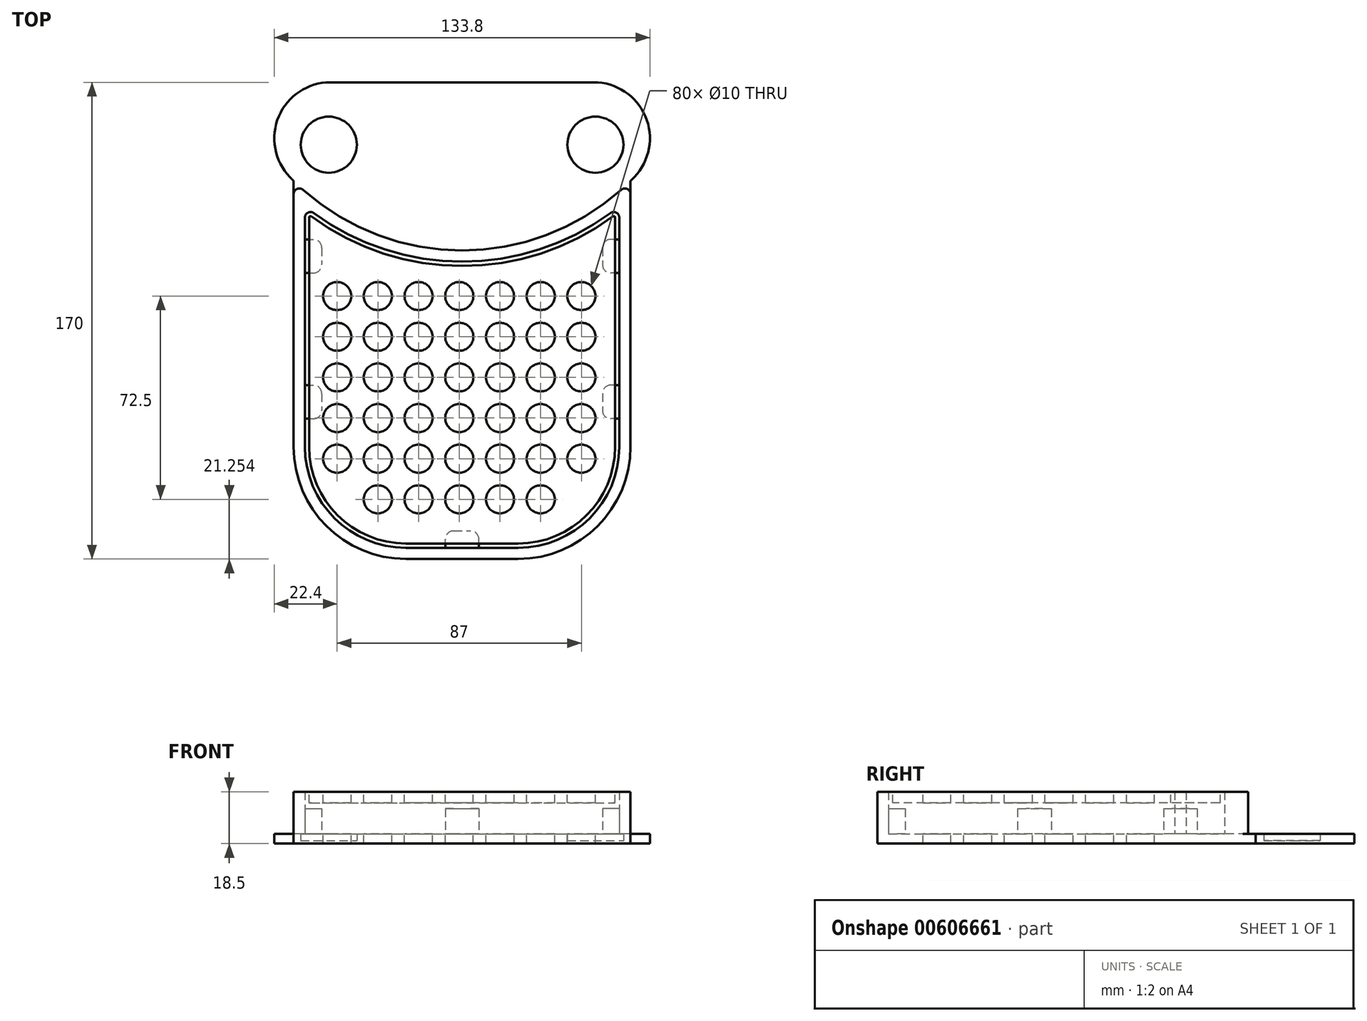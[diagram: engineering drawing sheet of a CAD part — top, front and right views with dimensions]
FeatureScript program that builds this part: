
annotation { "Feature Type Name" : "Feature", "Feature Type Description" : "" }
export const myFeature = defineFeature(function(context is Context, id is Id, definition is map)
    precondition{}
    {
        {
            var Q0;
            Q0=qCreatedBy(makeId("Top.planeOp"),FACE);
            var sketch = newSketch(context, id + "F0", { "sketchPlane" : qUnion([Q0])});
            skArc(sketch, "E0", {"start": v(-61.34, -58.85) * mm, "mid": v(-60.67, -59.53) * mm, "end": v(-60, -60.2) * mm});
            skCircle(sketch, "E1", {"center": v(-47.5, -47.25) * mm, "radius": 10 * mm});
            skCircle(sketch, "E2", {"center": v(47.5, -47.25) * mm, "radius": 10 * mm});
            skLineSegment(sketch, "E3", {"start": v(-60, -60.2) * mm, "end": v(-60, -155) * mm});
            skLineSegment(sketch, "E4", {"start": v(-20, -195) * mm, "end": v(20, -195) * mm});
            skLineSegment(sketch, "E5", {"start": v(60, -155) * mm, "end": v(60, -60.2) * mm});
            skLineSegment(sketch, "E6", {"start": v(-46.9, -25) * mm, "end": v(46.9, -25) * mm});
            skPoint(sketch, "E7.visualSharp", {"position": v(-81.24, -25) * mm});
            skArc(sketch, "E7.filletArc", {"start": v(-46.9, -25) * mm, "mid": v(-65.3, -37.16) * mm, "end": v(-61.34, -58.85) * mm});
            skPoint(sketch, "E8.visualSharp", {"position": v(81.24, -25) * mm});
            skArc(sketch, "E8.filletArc", {"start": v(61.34, -58.85) * mm, "mid": v(65.3, -37.16) * mm, "end": v(46.9, -25) * mm});
            skArc(sketch, "E9.trimOffspring", {"start": v(60, -60.2) * mm, "mid": v(60.67, -59.53) * mm, "end": v(61.34, -58.85) * mm});
            skPoint(sketch, "E10.visualSharp", {"position": v(-60, -195) * mm});
            skArc(sketch, "E10.filletArc", {"start": v(-60, -155) * mm, "mid": v(-48.28, -183.28) * mm, "end": v(-20, -195) * mm});
            skPoint(sketch, "E11.visualSharp", {"position": v(60, -195) * mm});
            skArc(sketch, "E11.filletArc", {"start": v(20, -195) * mm, "mid": v(48.28, -183.28) * mm, "end": v(60, -155) * mm});
            skSolve(sketch);
        }
        {
            var Q0;
            Q0 = qSketchRegion(id + "F0", true);
            extrude(context, id + "F1", {"entities" : qUnion([Q0]), "depth" : 3.5 * mm, "offsetDistance" : 25 * mm});
        }
        {
            var Q0;
            Q0=makeQuery(id+"F1.opExtrude","CAP_FACE",FACE,{"disambiguationData":[OSD([sQuery(id+"F0.wireOp",EDGE,"E0"),sQuery(id+"F0.wireOp",EDGE,"E1"),sQuery(id+"F0.wireOp",EDGE,"E2"),sQuery(id+"F0.wireOp",EDGE,"E3"),sQuery(id+"F0.wireOp",EDGE,"E4"),sQuery(id+"F0.wireOp",EDGE,"E5"),sQuery(id+"F0.wireOp",EDGE,"E6"),sQuery(id+"F0.wireOp",EDGE,"E7.filletArc"),sQuery(id+"F0.wireOp",EDGE,"E8.filletArc"),sQuery(id+"F0.wireOp",EDGE,"E9.trimOffspring"),sQuery(id+"F0.wireOp",EDGE,"E10.filletArc"),sQuery(id+"F0.wireOp",EDGE,"E11.filletArc")])],"isStart":true});
            var sketch = newSketch(context, id + "F2", { "sketchPlane" : qUnion([Q0])});
            skCircle(sketch, "E12", {"center": v(47.5, 47.25) * mm, "radius": 12.5 * mm});
            skCircle(sketch, "E13", {"center": v(-47.5, 47.25) * mm, "radius": 12.5 * mm});
            skSolve(sketch);
        }
        {
            var Q0;
            Q0 = qSketchRegion(id + "F2", true);
            extrude(context, id + "F3", {"entities" : qUnion([Q0]), "operationType" : NewBodyOperationType.ADD, "oppositeDirection" : true, "depth" : 1 * mm, "offsetDistance" : 25 * mm});
        }
        {
            var Q0;
            Q0=makeQuery(id+"F1.opExtrude","CAP_FACE",FACE,{"disambiguationData":[OSD([sQuery(id+"F0.wireOp",EDGE,"E0"),sQuery(id+"F0.wireOp",EDGE,"E1"),sQuery(id+"F0.wireOp",EDGE,"E2"),sQuery(id+"F0.wireOp",EDGE,"E3"),sQuery(id+"F0.wireOp",EDGE,"E4"),sQuery(id+"F0.wireOp",EDGE,"E5"),sQuery(id+"F0.wireOp",EDGE,"E6"),sQuery(id+"F0.wireOp",EDGE,"E7.filletArc"),sQuery(id+"F0.wireOp",EDGE,"E8.filletArc"),sQuery(id+"F0.wireOp",EDGE,"E9.trimOffspring"),sQuery(id+"F0.wireOp",EDGE,"E10.filletArc"),sQuery(id+"F0.wireOp",EDGE,"E11.filletArc")])],"isStart":false});
            var sketch = newSketch(context, id + "F4", { "sketchPlane" : qUnion([Q0])});
            skLineSegment(sketch, "E14.0", {"start": v(60, -155) * mm, "end": v(60, -64.85) * mm});
            skLineSegment(sketch, "E14.1", {"start": v(-60, -64.85) * mm, "end": v(-60, -155) * mm});
            skArc(sketch, "E14.2", {"start": v(-60, -155) * mm, "mid": v(-48.28, -183.28) * mm, "end": v(-20, -195) * mm});
            skLineSegment(sketch, "E14.3", {"start": v(-20, -195) * mm, "end": v(20, -195) * mm});
            skArc(sketch, "E14.4", {"start": v(20, -195) * mm, "mid": v(48.28, -183.28) * mm, "end": v(60, -155) * mm});
            skArc(sketch, "E15", {"start": v(-56.67, -63.36) * mm, "mid": v(0, -85) * mm, "end": v(56.67, -63.36) * mm});
            skLineSegment(sketch, "E16.0", {"start": v(-56, -73.25) * mm, "end": v(-56, -155) * mm});
            skLineSegment(sketch, "E16.1", {"start": v(56, -155) * mm, "end": v(56, -73.25) * mm});
            skArc(sketch, "E16.2", {"start": v(20, -191) * mm, "mid": v(45.46, -180.46) * mm, "end": v(56, -155) * mm});
            skArc(sketch, "E16.3", {"start": v(-52.81, -71.64) * mm, "mid": v(0, -89) * mm, "end": v(52.81, -71.64) * mm});
            skLineSegment(sketch, "E16.4", {"start": v(-20, -191) * mm, "end": v(20, -191) * mm});
            skArc(sketch, "E16.5", {"start": v(-56, -155) * mm, "mid": v(-45.46, -180.46) * mm, "end": v(-20, -191) * mm});
            skPoint(sketch, "E17.visualSharp", {"position": v(56, -69.17) * mm});
            skArc(sketch, "E17.filletArc", {"start": v(56, -73.25) * mm, "mid": v(54.9, -71.46) * mm, "end": v(52.81, -71.64) * mm});
            skPoint(sketch, "E18.visualSharp", {"position": v(60, -60.2) * mm});
            skArc(sketch, "E18.filletArc", {"start": v(60, -64.85) * mm, "mid": v(58.82, -63.02) * mm, "end": v(56.67, -63.36) * mm});
            skPoint(sketch, "E19.visualSharp", {"position": v(-60, -60.2) * mm});
            skArc(sketch, "E19.filletArc", {"start": v(-56.67, -63.36) * mm, "mid": v(-58.82, -63.02) * mm, "end": v(-60, -64.85) * mm});
            skPoint(sketch, "E20.visualSharp", {"position": v(-56, -69.17) * mm});
            skArc(sketch, "E20.filletArc", {"start": v(-52.81, -71.64) * mm, "mid": v(-54.9, -71.46) * mm, "end": v(-56, -73.25) * mm});
            skSolve(sketch);
        }
        {
            var Q0;
            Q0 = qSketchRegion(id + "F4", true);
            extrude(context, id + "F5", {"entities" : qUnion([Q0]), "operationType" : NewBodyOperationType.ADD, "depth" : 15 * mm, "offsetDistance" : 25 * mm});
        }
        {
            var Q0;
            Q0=makeQuery(id+"F5.boolean.opBoolean","SPLIT",FACE,{"disambiguationData":[TD([makeQuery(id+"F5.opExtrude","SWEPT_FACE",FACE,{"disambiguationData":[OSD([sQuery(id+"F4.wireOp",EDGE,"E16.0")])]})])],"derivedFrom":makeQuery(id+"F1.opExtrude","CAP_FACE",FACE,{"disambiguationData":[OSD([sQuery(id+"F0.wireOp",EDGE,"E0"),sQuery(id+"F0.wireOp",EDGE,"E1"),sQuery(id+"F0.wireOp",EDGE,"E2"),sQuery(id+"F0.wireOp",EDGE,"E3"),sQuery(id+"F0.wireOp",EDGE,"E4"),sQuery(id+"F0.wireOp",EDGE,"E5"),sQuery(id+"F0.wireOp",EDGE,"E6"),sQuery(id+"F0.wireOp",EDGE,"E7.filletArc"),sQuery(id+"F0.wireOp",EDGE,"E8.filletArc"),sQuery(id+"F0.wireOp",EDGE,"E9.trimOffspring"),sQuery(id+"F0.wireOp",EDGE,"E10.filletArc"),sQuery(id+"F0.wireOp",EDGE,"E11.filletArc")])],"isStart":false})});
            var sketch = newSketch(context, id + "F6", { "sketchPlane" : qUnion([Q0])});
            skLineSegment(sketch, "E21.bottom", {"start": v(-56, -81) * mm, "end": v(-53, -81) * mm});
            skLineSegment(sketch, "E21.top", {"start": v(-56, -93) * mm, "end": v(-53, -93) * mm});
            skLineSegment(sketch, "E21.left", {"start": v(-56, -81) * mm, "end": v(-56, -93) * mm});
            skLineSegment(sketch, "E21.right", {"start": v(-50, -84) * mm, "end": v(-50, -90) * mm});
            skLineSegment(sketch, "E22.bottom", {"start": v(-56, -133) * mm, "end": v(-53, -133) * mm});
            skLineSegment(sketch, "E22.top", {"start": v(-56, -145) * mm, "end": v(-53, -145) * mm});
            skLineSegment(sketch, "E22.left", {"start": v(-56, -133) * mm, "end": v(-56, -145) * mm});
            skLineSegment(sketch, "E22.right", {"start": v(-50, -136) * mm, "end": v(-50, -142) * mm});
            skLineSegment(sketch, "E23.bottom", {"start": v(0, -191) * mm, "end": v(-6, -191) * mm});
            skLineSegment(sketch, "E23.top", {"start": v(0, -185) * mm, "end": v(-3, -185) * mm});
            skLineSegment(sketch, "E23.right", {"start": v(-6, -191) * mm, "end": v(-6, -188) * mm});
            skPoint(sketch, "E24.visualSharp", {"position": v(-6, -185) * mm});
            skArc(sketch, "E24.filletArc", {"start": v(-3, -185) * mm, "mid": v(-5.12, -185.88) * mm, "end": v(-6, -188) * mm});
            skPoint(sketch, "E25.visualSharp", {"position": v(-50, -145) * mm});
            skArc(sketch, "E25.filletArc", {"start": v(-53, -145) * mm, "mid": v(-50.88, -144.12) * mm, "end": v(-50, -142) * mm});
            skPoint(sketch, "E26.visualSharp", {"position": v(-50, -133) * mm});
            skArc(sketch, "E26.filletArc", {"start": v(-50, -136) * mm, "mid": v(-50.88, -133.88) * mm, "end": v(-53, -133) * mm});
            skPoint(sketch, "E27.visualSharp", {"position": v(-50, -93) * mm});
            skArc(sketch, "E27.filletArc", {"start": v(-53, -93) * mm, "mid": v(-50.88, -92.12) * mm, "end": v(-50, -90) * mm});
            skPoint(sketch, "E28.visualSharp", {"position": v(-50, -81) * mm});
            skArc(sketch, "E28.filletArc", {"start": v(-50, -84) * mm, "mid": v(-50.88, -81.88) * mm, "end": v(-53, -81) * mm});
            skLineSegment(sketch, "E29.MirrorCS", {"start": v(6, -191) * mm, "end": v(6, -188) * mm});
            skArc(sketch, "E30.MirrorCS", {"start": v(3, -185) * mm, "mid": v(5.12, -185.88) * mm, "end": v(6, -188) * mm});
            skLineSegment(sketch, "E31.MirrorCS", {"start": v(0, -185) * mm, "end": v(3, -185) * mm});
            skArc(sketch, "E32.MirrorCS", {"start": v(53, -145) * mm, "mid": v(50.88, -144.12) * mm, "end": v(50, -142) * mm});
            skLineSegment(sketch, "E33.MirrorCS", {"start": v(50, -136) * mm, "end": v(50, -142) * mm});
            skLineSegment(sketch, "E34.MirrorCS", {"start": v(56, -145) * mm, "end": v(53, -145) * mm});
            skLineSegment(sketch, "E35.MirrorCS", {"start": v(56, -133) * mm, "end": v(53, -133) * mm});
            skLineSegment(sketch, "E36.MirrorCS", {"start": v(50, -84) * mm, "end": v(50, -90) * mm});
            skArc(sketch, "E37.MirrorCS", {"start": v(50, -136) * mm, "mid": v(50.88, -133.88) * mm, "end": v(53, -133) * mm});
            skLineSegment(sketch, "E38.MirrorCS", {"start": v(56, -81) * mm, "end": v(53, -81) * mm});
            skArc(sketch, "E39.MirrorCS", {"start": v(50, -84) * mm, "mid": v(50.88, -81.88) * mm, "end": v(53, -81) * mm});
            skArc(sketch, "E40.MirrorCS", {"start": v(53, -93) * mm, "mid": v(50.88, -92.12) * mm, "end": v(50, -90) * mm});
            skLineSegment(sketch, "E41.MirrorCS", {"start": v(56, -93) * mm, "end": v(53, -93) * mm});
            skLineSegment(sketch, "E42.MirrorCS", {"start": v(56, -133) * mm, "end": v(56, -145) * mm});
            skLineSegment(sketch, "E43.MirrorCS", {"start": v(56, -81) * mm, "end": v(56, -93) * mm});
            skLineSegment(sketch, "E44.MirrorCS", {"start": v(0, -191) * mm, "end": v(6, -191) * mm});
            skPoint(sketch, "E45.MirrorP", {"position": v(50, -145) * mm});
            skPoint(sketch, "E46.MirrorP", {"position": v(50, -81) * mm});
            skPoint(sketch, "E47.MirrorP", {"position": v(6, -185) * mm});
            skPoint(sketch, "E48.MirrorP", {"position": v(50, -93) * mm});
            skPoint(sketch, "E49.MirrorP", {"position": v(50, -133) * mm});
            skSolve(sketch);
        }
        {
            var Q0;
            Q0 = qSketchRegion(id + "F6", true);
            extrude(context, id + "F7", {"entities" : qUnion([Q0]), "operationType" : NewBodyOperationType.ADD, "depth" : 9 * mm, "offsetDistance" : 25 * mm});
        }
        {
            var Q0;
            Q0=makeQuery(id+"F5.opExtrude","CAP_FACE",FACE,{"disambiguationData":[OSD([sQuery(id+"F4.wireOp",EDGE,"E14.0"),sQuery(id+"F4.wireOp",EDGE,"E14.1"),sQuery(id+"F4.wireOp",EDGE,"E14.2"),sQuery(id+"F4.wireOp",EDGE,"E14.3"),sQuery(id+"F4.wireOp",EDGE,"E14.4"),sQuery(id+"F4.wireOp",EDGE,"E15"),sQuery(id+"F4.wireOp",EDGE,"E16.0"),sQuery(id+"F4.wireOp",EDGE,"E16.1"),sQuery(id+"F4.wireOp",EDGE,"E16.2"),sQuery(id+"F4.wireOp",EDGE,"E16.3"),sQuery(id+"F4.wireOp",EDGE,"E16.4"),sQuery(id+"F4.wireOp",EDGE,"E16.5"),sQuery(id+"F4.wireOp",EDGE,"E17.filletArc"),sQuery(id+"F4.wireOp",EDGE,"E18.filletArc"),sQuery(id+"F4.wireOp",EDGE,"E19.filletArc"),sQuery(id+"F4.wireOp",EDGE,"E20.filletArc")])],"isStart":false});
            var sketch = newSketch(context, id + "F8", { "sketchPlane" : qUnion([Q0])});
            skArc(sketch, "E50.0", {"start": v(-53.7, -72.84) * mm, "mid": v(-54.23, -72.8) * mm, "end": v(-54.5, -73.25) * mm});
            skArc(sketch, "E50.1", {"start": v(-53.7, -72.84) * mm, "mid": v(0, -90.5) * mm, "end": v(53.7, -72.84) * mm});
            skLineSegment(sketch, "E50.2", {"start": v(-54.5, -73.25) * mm, "end": v(-54.5, -140.3) * mm});
            skArc(sketch, "E50.3", {"start": v(54.5, -73.25) * mm, "mid": v(54.23, -72.8) * mm, "end": v(53.7, -72.84) * mm});
            skArc(sketch, "E50.6", {"start": v(20, -189.5) * mm, "mid": v(44.4, -179.4) * mm, "end": v(54.5, -155) * mm});
            skLineSegment(sketch, "E50.7", {"start": v(54.5, -155) * mm, "end": v(54.5, -73.25) * mm});
            skLineSegment(sketch, "E51", {"start": v(-54.5, -155) * mm, "end": v(-54.5, -140.3) * mm});
            skLineSegment(sketch, "E52", {"start": v(20, -189.5) * mm, "end": v(-20, -189.5) * mm});
            skPoint(sketch, "E53.visualSharp", {"position": v(-54.5, -189.5) * mm});
            skArc(sketch, "E53.filletArc", {"start": v(-54.5, -155) * mm, "mid": v(-44.4, -179.4) * mm, "end": v(-20, -189.5) * mm});
            skSolve(sketch);
        }
        {
            var Q0;
            Q0=makeQuery(id+"F8.imprint","IMPRINT",FACE,{"disambiguationData":[TD([[makeQuery(id+"F8.imprint","IMPRINT",EDGE,{"derivedFrom":sQuery(id+"F8.wireOp",EDGE,"E50.0")}),1.0]])]});
            extrude(context, id + "F9", {"entities" : qUnion([Q0]), "oppositeDirection" : true, "depth" : 4 * mm, "offsetDistance" : 25 * mm});
        }
        {
            var Q0;
            Q0=makeQuery(id+"F9.opExtrude","CAP_FACE",FACE,{"disambiguationData":[OSD([sQuery(id+"F8.wireOp",EDGE,"E50.0"),sQuery(id+"F8.wireOp",EDGE,"E50.1"),sQuery(id+"F8.wireOp",EDGE,"E50.2"),sQuery(id+"F8.wireOp",EDGE,"E50.3"),sQuery(id+"F8.wireOp",EDGE,"E50.4"),sQuery(id+"F8.wireOp",EDGE,"E50.5"),sQuery(id+"F8.wireOp",EDGE,"E50.6"),sQuery(id+"F8.wireOp",EDGE,"E50.7")])],"isStart":true});
            var sketch = newSketch(context, id + "F10", { "sketchPlane" : qUnion([Q0])});
            skCircle(sketch, "E54", {"center": v(-44.5, -101.25) * mm, "radius": 5 * mm});
            skCircle(sketch, "E55.0.1.0", {"center": v(-44.5, -115.75) * mm, "radius": 5 * mm});
            skCircle(sketch, "E55.0.2.0", {"center": v(-44.5, -130.25) * mm, "radius": 5 * mm});
            skCircle(sketch, "E55.0.3.0", {"center": v(-44.5, -144.75) * mm, "radius": 5 * mm});
            skCircle(sketch, "E55.0.4.0", {"center": v(-44.5, -159.25) * mm, "radius": 5 * mm});
            skCircle(sketch, "E55.1.0.0", {"center": v(-30, -101.25) * mm, "radius": 5 * mm});
            skCircle(sketch, "E55.1.1.0", {"center": v(-30, -115.75) * mm, "radius": 5 * mm});
            skCircle(sketch, "E55.1.2.0", {"center": v(-30, -130.25) * mm, "radius": 5 * mm});
            skCircle(sketch, "E55.1.3.0", {"center": v(-30, -144.75) * mm, "radius": 5 * mm});
            skCircle(sketch, "E55.1.4.0", {"center": v(-30, -159.25) * mm, "radius": 5 * mm});
            skCircle(sketch, "E55.2.0.0", {"center": v(-15.5, -101.25) * mm, "radius": 5 * mm});
            skCircle(sketch, "E55.2.1.0", {"center": v(-15.5, -115.75) * mm, "radius": 5 * mm});
            skCircle(sketch, "E55.2.2.0", {"center": v(-15.5, -130.25) * mm, "radius": 5 * mm});
            skCircle(sketch, "E55.2.3.0", {"center": v(-15.5, -144.75) * mm, "radius": 5 * mm});
            skCircle(sketch, "E55.2.4.0", {"center": v(-15.5, -159.25) * mm, "radius": 5 * mm});
            skCircle(sketch, "E55.3.0.0", {"center": v(-1, -101.25) * mm, "radius": 5 * mm});
            skCircle(sketch, "E55.3.1.0", {"center": v(-1, -115.75) * mm, "radius": 5 * mm});
            skCircle(sketch, "E55.3.2.0", {"center": v(-1, -130.25) * mm, "radius": 5 * mm});
            skCircle(sketch, "E55.3.3.0", {"center": v(-1, -144.75) * mm, "radius": 5 * mm});
            skCircle(sketch, "E55.3.4.0", {"center": v(-1, -159.25) * mm, "radius": 5 * mm});
            skCircle(sketch, "E55.4.0.0", {"center": v(13.5, -101.25) * mm, "radius": 5 * mm});
            skCircle(sketch, "E55.4.1.0", {"center": v(13.5, -115.75) * mm, "radius": 5 * mm});
            skCircle(sketch, "E55.4.2.0", {"center": v(13.5, -130.25) * mm, "radius": 5 * mm});
            skCircle(sketch, "E55.4.3.0", {"center": v(13.5, -144.75) * mm, "radius": 5 * mm});
            skCircle(sketch, "E55.4.4.0", {"center": v(13.5, -159.25) * mm, "radius": 5 * mm});
            skCircle(sketch, "E55.5.0.0", {"center": v(28, -101.25) * mm, "radius": 5 * mm});
            skCircle(sketch, "E55.5.1.0", {"center": v(28, -115.75) * mm, "radius": 5 * mm});
            skCircle(sketch, "E55.5.2.0", {"center": v(28, -130.25) * mm, "radius": 5 * mm});
            skCircle(sketch, "E55.5.3.0", {"center": v(28, -144.75) * mm, "radius": 5 * mm});
            skCircle(sketch, "E55.5.4.0", {"center": v(28, -159.25) * mm, "radius": 5 * mm});
            skCircle(sketch, "E55.6.0.0", {"center": v(42.5, -101.25) * mm, "radius": 5 * mm});
            skCircle(sketch, "E55.6.1.0", {"center": v(42.5, -115.75) * mm, "radius": 5 * mm});
            skCircle(sketch, "E55.6.2.0", {"center": v(42.5, -130.25) * mm, "radius": 5 * mm});
            skCircle(sketch, "E55.6.3.0", {"center": v(42.5, -144.75) * mm, "radius": 5 * mm});
            skCircle(sketch, "E55.6.4.0", {"center": v(42.5, -159.25) * mm, "radius": 5 * mm});
            skLineSegment(sketch, "E55.direction1", {"start": v(-44.5, -101.25) * mm, "end": v(-30, -101.25) * mm, "construction": true});
            skLineSegment(sketch, "E55.direction2", {"start": v(-44.5, -101.25) * mm, "end": v(-44.5, -115.75) * mm, "construction": true});
            skCircle(sketch, "E56.0.1.5", {"center": v(-30, -173.75) * mm, "radius": 5 * mm});
            skCircle(sketch, "E56.0.2.5", {"center": v(-15.5, -173.75) * mm, "radius": 5 * mm});
            skCircle(sketch, "E56.0.3.5", {"center": v(-1, -173.75) * mm, "radius": 5 * mm});
            skCircle(sketch, "E56.0.4.5", {"center": v(13.5, -173.75) * mm, "radius": 5 * mm});
            skCircle(sketch, "E56.0.5.5", {"center": v(28, -173.75) * mm, "radius": 5 * mm});
            skSolve(sketch);
        }
        {
            var Q0;
            Q0 = qSketchRegion(id + "F10", true);
            extrude(context, id + "F11", {"entities" : qUnion([Q0]), "operationType" : NewBodyOperationType.REMOVE, "oppositeDirection" : true, "depth" : 25 * mm, "offsetDistance" : 25 * mm});
        }
    });
